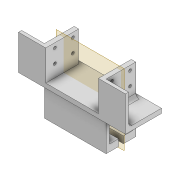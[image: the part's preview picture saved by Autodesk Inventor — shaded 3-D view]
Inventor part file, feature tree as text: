
AUTODESK INVENTOR PART (.ipt)
format: ipt  version: 2022 (Build 260153000, 153)  size: 204,288 bytes
history: native  units: mm
features: extrude x5, sketch x5, projected_geometry x3, plane x1, fillet x1
ambient origin geometry x8: Origin, YZ Plane, XZ Plane, XY Plane, X Axis, Y Axis, Z Axis, Center Point
bodies: Solid1 (feature_tree)
feature tree (15):
  extrude  "Extrusion1"  Depth=20.4mm
  extrude  "Extrusion11"  Depth=54.8mm TaperAngle=0.0deg
  extrude  "Extrusion12"  Depth=3.0mm
  plane  "Work Plane1"
  extrude  "Extrusion13"  Depth=8.0mm
  extrude  "Extrusion14"  Depth=4.0mm
  fillet  "Fillet5"  Radius=4.0mm
  sketch  "Sketch2"  dims[d5=20.4mm d6=20.4mm]
  sketch  "Sketch13"  dims[d8=6.0mm d9=54.8mm d10=0.0mm]
  sketch  "Sketch14"  dims[d22=4.0mm d23=3.0mm]
  sketch  "Sketch15"  dims[d24=3.0mm d27=8.0mm]
  projected_geometry  "Projected Loop12"
  sketch  "Sketch16"  dims[d28=8.0mm d75=4.0mm d76=4.0mm d77=46.8mm d78=27.0mm d79=0.0mm d80=2.6mm d82=2.6mm d86=2.6mm d87=2.6mm d92=100.0mm d93=0.0mm d95=16.0mm d96=16.0mm d97=5.2mm d98=5.2mm d99=5.2mm d100=5.2mm d101=11.0mm d102=23.0mm d103=32.0mm d104=20.0mm d105=75.0mm d106=0.0mm d107=0.0mm d108=27.0mm d109=0.0mm d110=3.0mm]
  projected_geometry  "Projected Loop13"
  projected_geometry  "Projected Loop14"
